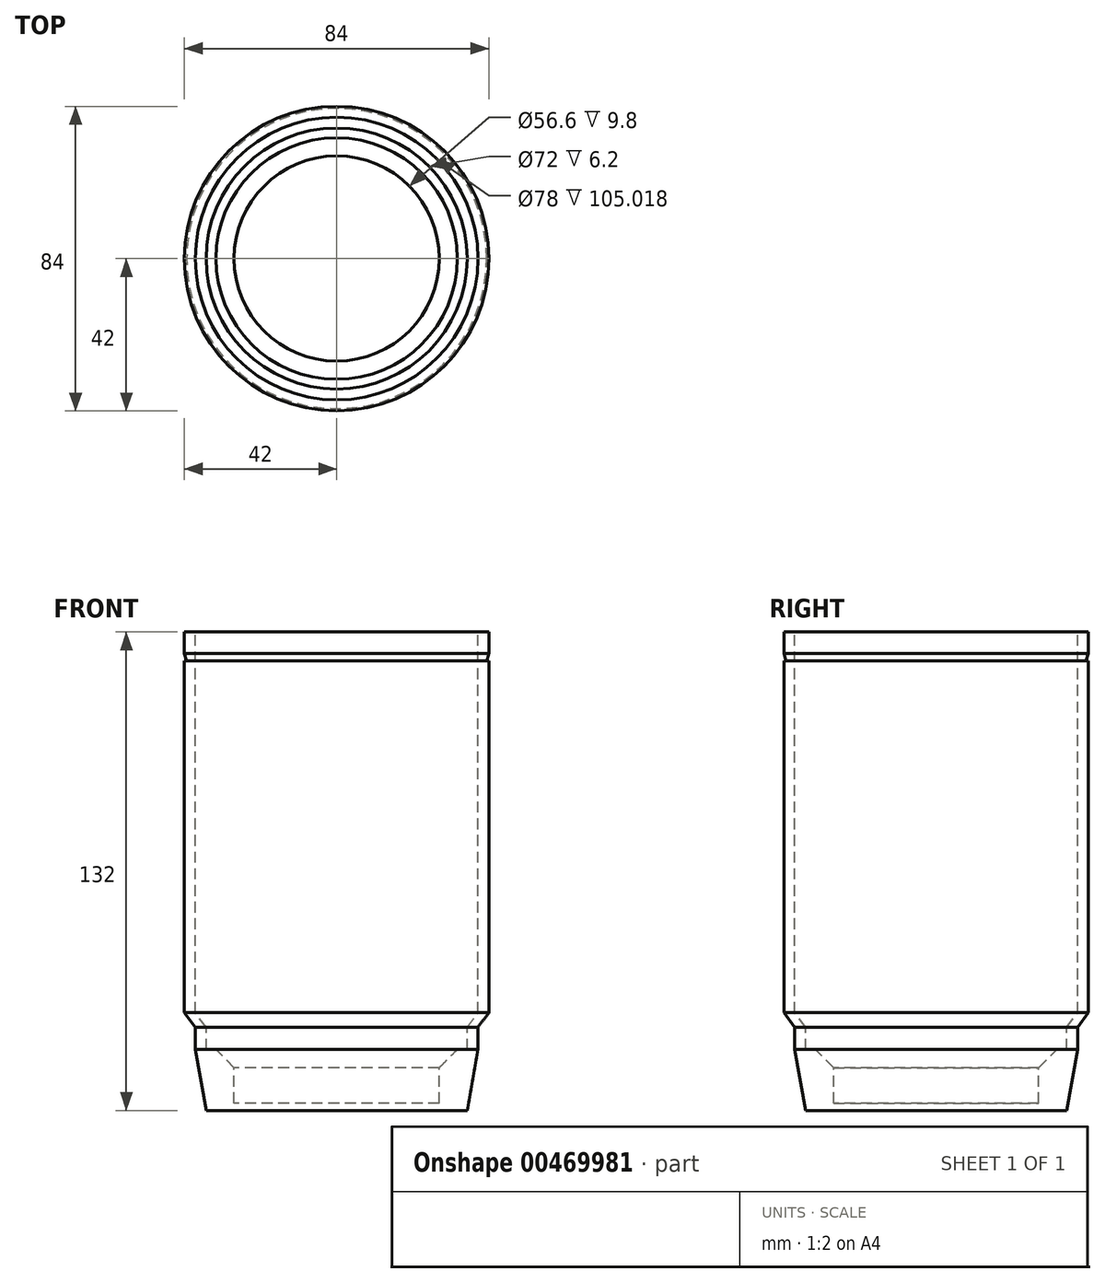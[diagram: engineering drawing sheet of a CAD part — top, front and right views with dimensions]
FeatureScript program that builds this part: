
annotation { "Feature Type Name" : "Feature", "Feature Type Description" : "" }
export const myFeature = defineFeature(function(context is Context, id is Id, definition is map)
    precondition{}
    {
        {
            var Q0;
            Q0=qCreatedBy(makeId("Front.planeOp"),FACE);
            var sketch = newSketch(context, id + "F0", { "sketchPlane" : qUnion([Q0])});
            skLineSegment(sketch, "E0", {"start": v(0, 0) * mm, "end": v(-28.3, 0) * mm});
            skLineSegment(sketch, "E1", {"start": v(-28.3, 0) * mm, "end": v(-28.3, 9.8) * mm});
            skLineSegment(sketch, "E2.bottom", {"start": v(0, 0) * mm, "end": v(-36, 0) * mm, "construction": true});
            skLineSegment(sketch, "E2.top", {"start": v(0, 21) * mm, "end": v(-36, 21) * mm, "construction": true});
            skLineSegment(sketch, "E2.left", {"start": v(0, 0) * mm, "end": v(0, 21) * mm, "construction": true});
            skLineSegment(sketch, "E2.right", {"start": v(-36, 0) * mm, "end": v(-36, 21) * mm, "construction": true});
            skLineSegment(sketch, "E3", {"start": v(-36, 21) * mm, "end": v(-36, 14.8) * mm});
            skLineSegment(sketch, "E4", {"start": v(-36, 14.8) * mm, "end": v(-33.3, 14.8) * mm});
            skLineSegment(sketch, "E5.bottom", {"start": v(0, 0) * mm, "end": v(-39, 0) * mm, "construction": true});
            skLineSegment(sketch, "E5.top", {"start": v(0, 130) * mm, "end": v(-39, 130) * mm, "construction": true});
            skLineSegment(sketch, "E5.left", {"start": v(0, 0) * mm, "end": v(0, 130) * mm, "construction": true});
            skLineSegment(sketch, "E5.right", {"start": v(-39, 0) * mm, "end": v(-39, 130) * mm, "construction": true});
            skLineSegment(sketch, "E6", {"start": v(-36, 21) * mm, "end": v(-39, 24.98) * mm});
            skLineSegment(sketch, "E7", {"start": v(-39, 24.98) * mm, "end": v(-39, 130) * mm});
            skLineSegment(sketch, "E8", {"start": v(-39, 130) * mm, "end": v(-42, 130) * mm});
            skLineSegment(sketch, "E9", {"start": v(-42, 130) * mm, "end": v(-42, 124) * mm});
            skLineSegment(sketch, "E10.bottom", {"start": v(-39, 130) * mm, "end": v(-41.4, 130) * mm, "construction": true});
            skLineSegment(sketch, "E10.top", {"start": v(-39, 122) * mm, "end": v(-41.4, 122) * mm, "construction": true});
            skLineSegment(sketch, "E10.left", {"start": v(-39, 130) * mm, "end": v(-39, 122) * mm, "construction": true});
            skLineSegment(sketch, "E10.right", {"start": v(-41.4, 130) * mm, "end": v(-41.4, 122) * mm, "construction": true});
            skLineSegment(sketch, "E11", {"start": v(-42, 124) * mm, "end": v(-41.4, 122) * mm});
            skLineSegment(sketch, "E12", {"start": v(-42, 122) * mm, "end": v(-42, 24.98) * mm});
            skLineSegment(sketch, "E13", {"start": v(-42, 24.98) * mm, "end": v(-39, 21) * mm});
            skLineSegment(sketch, "E14", {"start": v(-39, 21) * mm, "end": v(-39, 14.8) * mm});
            skLineSegment(sketch, "E15", {"start": v(-36, 17.9) * mm, "end": v(-39, 17.9) * mm, "construction": true});
            skLineSegment(sketch, "E16", {"start": v(0, 0) * mm, "end": v(0, -2) * mm});
            skLineSegment(sketch, "E17", {"start": v(0, -2) * mm, "end": v(-28.3, -2) * mm});
            skLineSegment(sketch, "E18", {"start": v(-39, 14.8) * mm, "end": v(-36, -2) * mm});
            skLineSegment(sketch, "E19", {"start": v(-36, -2) * mm, "end": v(-28.3, -2) * mm});
            skLineSegment(sketch, "E20", {"start": v(-33.3, 14.8) * mm, "end": v(-28.3, 9.8) * mm});
            skLineSegment(sketch, "E21", {"start": v(-42, 122) * mm, "end": v(-41.4, 122) * mm});
            skSolve(sketch);
        }
        {
            var Q0;
            Q0=makeQuery(id+"F0.imprint","IMPRINT",FACE,{"disambiguationData":[TD([[makeQuery(id+"F0.imprint","IMPRINT",EDGE,{"derivedFrom":sQuery(id+"F0.wireOp",EDGE,"E0")}),1.0]])]});
            var Q1;
            Q1=sQuery(id+"F0.wireOp",EDGE,"E16");
            revolve(context, id + "F1", {"entities" : qUnion([Q0]), "axis" : qUnion([Q1]), "revolveType" : RevolveType.FULL});
        }
    });
